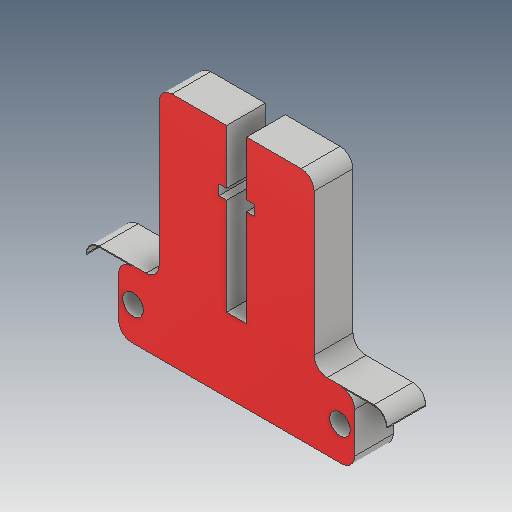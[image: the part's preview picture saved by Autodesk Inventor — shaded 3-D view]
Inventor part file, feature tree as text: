
AUTODESK INVENTOR PART (.ipt)
format: ipt  version: 2017 (Build 210142000, 142)  size: 379,392 bytes
history: native  units: in
note: dims shown in document units (in); Inventor stores cm internally (conversion verified against a paired STEP export)
features: extrude x5, sketch x5, projected_geometry x3, fillet x1
ambient origin geometry x8: Origin, YZ Plane, XZ Plane, XY Plane, X Axis, Y Axis, Z Axis, Center Point
bodies: Solid1 (feature_tree)
feature tree (14):
  extrude  "Extrusion1"  Depth=0.0787in
  extrude  "Extrusion2"  Depth=0.2362in TaperAngle=0.0deg
  fillet  "Fillet1"  Radius=0.0787in
  sketch  "Sketch3"  dims[d4=0.2362in d5=0.0in d6=0.2362in d7=0.0in d8=0.0787in]
  extrude  "Extrusion3"  Depth=0.0157in TaperAngle=0.0deg
  extrude  "Extrusion4"  [1 undecoded]
  extrude  "Extrusion5"  [1 undecoded]
  sketch  "Sketch1"  dims[d0=0.9449in d1=0.126in d2=0.126in d3=0.0787in]
  sketch  "Sketch4"  dims[d10=0.5118in d11=0.0in d12=0.0157in d13=0.0in]
  projected_geometry  "Projected Loop1"
  sketch  "Sketch5"  dims[d14=0.0039in d15=0.0in]
  projected_geometry  "Projected Loop2"
  projected_geometry  "Projected Loop3"
  sketch  "Sketch6"
note: 2 required parameter values undecoded (feature->parameter linkage not recoverable at this tier; creation-order binding heuristic only, values carry confidence <= 0.55)
